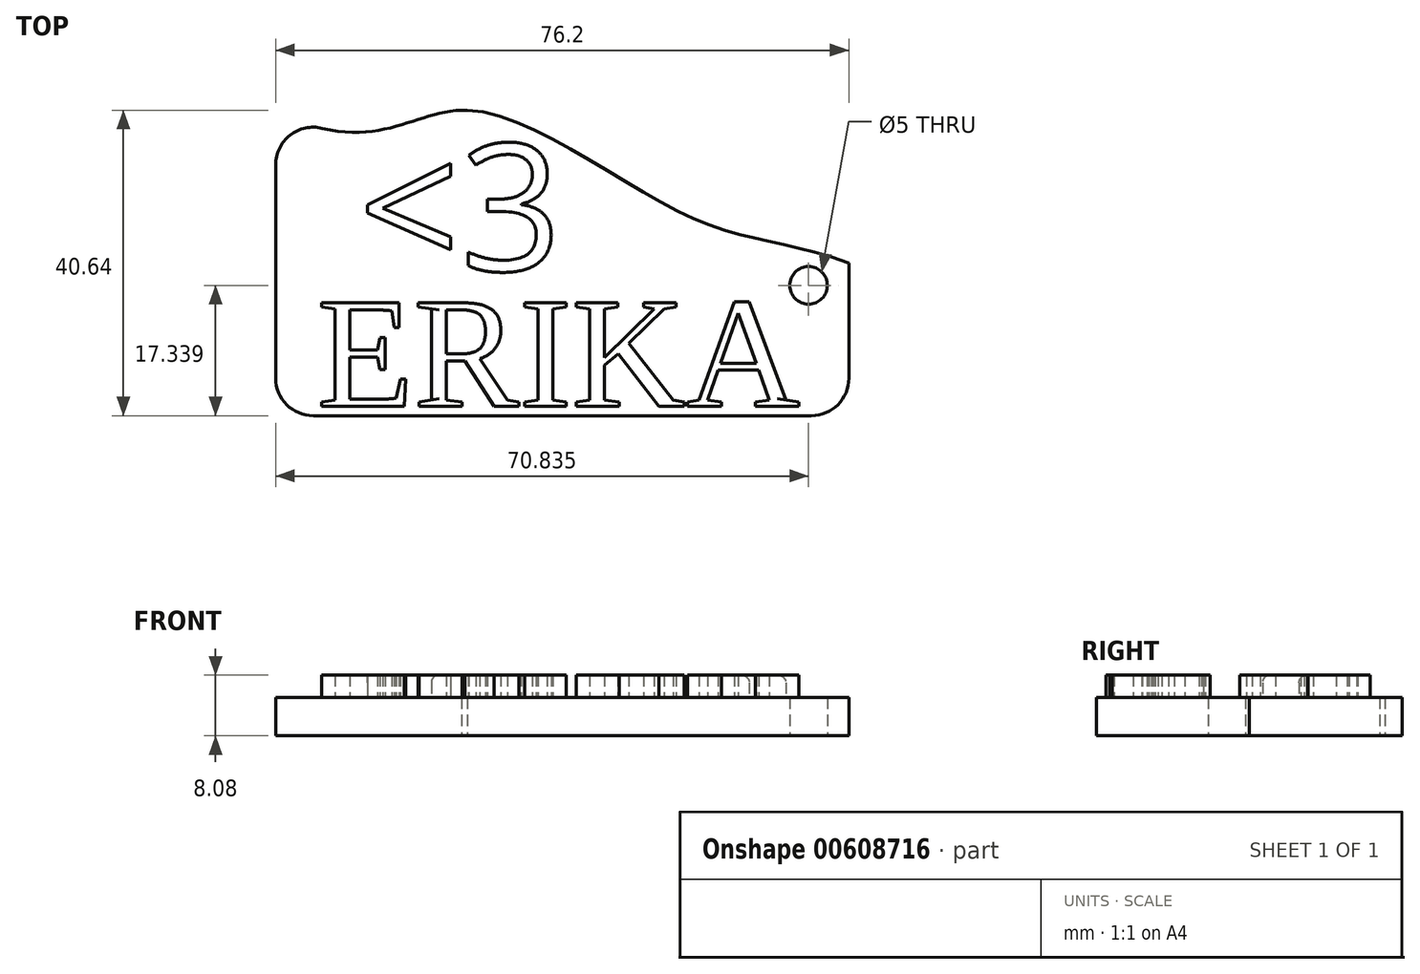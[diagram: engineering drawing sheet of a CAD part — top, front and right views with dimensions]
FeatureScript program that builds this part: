
annotation { "Feature Type Name" : "Feature", "Feature Type Description" : "" }
export const myFeature = defineFeature(function(context is Context, id is Id, definition is map)
    precondition{}
    {
        {
            var Q0;
            Q0=qCreatedBy(makeId("Top.planeOp"),FACE);
            var sketch = newSketch(context, id + "F0", { "sketchPlane" : qUnion([Q0])});
            skLineSegment(sketch, "E0.bottom", {"start": v(0, 0) * mm, "end": v(381, 0) * mm});
            skLineSegment(sketch, "E0.top", {"start": v(0, 203.2) * mm, "end": v(381, 203.2) * mm});
            skLineSegment(sketch, "E0.left", {"start": v(0, 0) * mm, "end": v(0, 203.2) * mm});
            skLineSegment(sketch, "E0.right", {"start": v(381, 0) * mm, "end": v(381, 203.2) * mm});
            skSolve(sketch);
        }
        {
            var Q0;
            Q0=makeQuery(id+"F0.imprint","IMPRINT",FACE,{"disambiguationData":[TD([[makeQuery(id+"F0.imprint","IMPRINT",EDGE,{"derivedFrom":sQuery(id+"F0.wireOp",EDGE,"E0.bottom")}),1.0]])]});
            extrude(context, id + "F1", {"entities" : qUnion([Q0]), "depth" : 25.4 * mm, "offsetDistance" : 25.4 * mm});
        }
        {
            var Q0;
            Q0=makeQuery(id+"F1.opExtrude","CAP_FACE",FACE,{"disambiguationData":[OSD([sQuery(id+"F0.wireOp",EDGE,"E0.bottom"),sQuery(id+"F0.wireOp",EDGE,"E0.top"),sQuery(id+"F0.wireOp",EDGE,"E0.left"),sQuery(id+"F0.wireOp",EDGE,"E0.right")])],"isStart":false});
            var sketch = newSketch(context, id + "F2", { "sketchPlane" : qUnion([Q0])});
            skText(sketch, "E1", { "text": "ERIKA", "fontName": "Tinos-Regular.ttf"});
            const initialGuessF2  = {"E1": [0.02744, 0.00627, 1, 0, 0.07568]};
            skSetInitialGuess(sketch, initialGuessF2);
            skSolve(sketch);
        }
        {
            var Q0;
            Q0=makeQuery(id+"F2.imprint","IMPRINT",FACE,{"disambiguationData":[TD([[makeQuery(id+"F2.imprint","IMPRINT",EDGE,{"derivedFrom":sQuery(id+"F2.wireOp",EDGE,"E1.sketch_text.stroke-26")}),-1.0]])]});
            var Q1;
            Q1=makeQuery(id+"F2.imprint","IMPRINT",FACE,{"disambiguationData":[TD([[makeQuery(id+"F2.imprint","IMPRINT",EDGE,{"derivedFrom":sQuery(id+"F2.wireOp",EDGE,"E1.sketch_text.stroke-53")}),-1.0]])]});
            var Q2;
            Q2=makeQuery(id+"F2.imprint","IMPRINT",FACE,{"disambiguationData":[TD([[makeQuery(id+"F2.imprint","IMPRINT",EDGE,{"derivedFrom":sQuery(id+"F2.wireOp",EDGE,"E1.sketch_text.stroke-65")}),-1.0]])]});
            var Q3;
            Q3=makeQuery(id+"F2.imprint","IMPRINT",FACE,{"disambiguationData":[TD([[makeQuery(id+"F2.imprint","IMPRINT",EDGE,{"derivedFrom":sQuery(id+"F2.wireOp",EDGE,"E1.sketch_text.stroke-91")}),-1.0]])]});
            var Q4;
            Q4=makeQuery(id+"F2.imprint","IMPRINT",FACE,{"disambiguationData":[TD([[makeQuery(id+"F2.imprint","IMPRINT",EDGE,{"derivedFrom":sQuery(id+"F2.wireOp",EDGE,"E1.sketch_text.stroke-0")}),-1.0]])]});
            extrude(context, id + "F3", {"entities" : qUnion([Q0, Q1, Q2, Q3, Q4]), "operationType" : NewBodyOperationType.ADD, "depth" : 15 * mm, "offsetDistance" : 25.4 * mm});
        }
        {
            var Q0;
            {var subQ0=sQuery(id+"F0.wireOp",EDGE,"E0.top");var subQ1=sQuery(id+"F0.wireOp",EDGE,"E0.right");var subQ2=sQuery(id+"F0.wireOp",EDGE,"E0.bottom");var subQ3=sQuery(id+"F0.wireOp",EDGE,"E0.left");Q0=makeQuery(id+"F3.boolean.opBoolean","SPLIT",FACE,{"disambiguationData":[TD([makeQuery(id+"F1.opExtrude","SWEPT_FACE",FACE,{"disambiguationData":[OSD([subQ2])]})])],"derivedFrom":makeQuery(id+"F1.opExtrude","CAP_FACE",FACE,{"disambiguationData":[OSD([subQ2,subQ0,subQ3,subQ1])],"isStart":false})});}
            var sketch = newSketch(context, id + "F4", { "sketchPlane" : qUnion([Q0])});
            skText(sketch, "E2", { "text": "<3", "fontName": "OpenSans-Regular.ttf"});
            const initialGuessF4  = {"E2": [0.055, 0.09643, 1, 0, 0.08502]};
            skSetInitialGuess(sketch, initialGuessF4);
            skSolve(sketch);
        }
        {
            var Q0;
            Q0 = qSketchRegion(id + "F4", true);
            extrude(context, id + "F5", {"entities" : qUnion([Q0]), "operationType" : NewBodyOperationType.ADD, "depth" : 15 * mm, "offsetDistance" : 25.4 * mm});
        }
        {
            var Q0;
            Q0=makeQuery(id+"F1.opExtrude","SWEPT_BODY",BODY,{"disambiguationData":[OSD([sQuery(id+"F0.wireOp",EDGE,"E0.bottom"),sQuery(id+"F0.wireOp",EDGE,"E0.top"),sQuery(id+"F0.wireOp",EDGE,"E0.left"),sQuery(id+"F0.wireOp",EDGE,"E0.right")])]});
            var Q1;
            Q1=qCreatedBy(makeId("Origin.pointOp"),VERTEX);
            transform(context, id + "F6", {"entities" : qUnion([Q0]), "transformType" : TransformType.SCALE_UNIFORMLY, "scale" : 0.2, "scalePoint" : qUnion([Q1]), "makeCopy" : false});
        }
        {
            var Q0;
            Q0=makeQuery(id+"F1.opExtrude","CAP_FACE",FACE,{"disambiguationData":[OSD([sQuery(id+"F0.wireOp",EDGE,"E0.bottom"),sQuery(id+"F0.wireOp",EDGE,"E0.top"),sQuery(id+"F0.wireOp",EDGE,"E0.left"),sQuery(id+"F0.wireOp",EDGE,"E0.right")])],"isStart":true});
            var sketch = newSketch(context, id + "F7", { "sketchPlane" : qUnion([Q0])});
            skPoint(sketch, "E3", {"position": v(76.2, -40.64) * mm});
            skFitSpline(sketch, "E4", {"points": [v(76.2, -20.32) * mm, v(54.58, -26.68) * mm, v(25.49, -40.64) * mm, v(0, -40.64) * mm], "startDerivative": vector(-82.52, -29.2) * mm, "endDerivative": vector(-119.64, -62.23) * mm});
            skLineSegment(sketch, "E5", {"start": v(76.2, -20.32) * mm, "end": v(76.2, -49.02) * mm});
            skLineSegment(sketch, "E6", {"start": v(76.2, -49.02) * mm, "end": v(0, -40.64) * mm});
            skCircle(sketch, "E7", {"center": v(70.83, -17.34) * mm, "radius": 2.5 * mm});
            skSolve(sketch);
        }
        {
            var Q0;
            Q0 = qSketchRegion(id + "F7", true);
            extrude(context, id + "F8", {"entities" : qUnion([Q0]), "operationType" : NewBodyOperationType.REMOVE, "oppositeDirection" : true, "depth" : 25 * mm, "offsetDistance" : 25 * mm});
        }
        {
            var Q0;
            {var subQ0=sQuery(id+"F0.wireOp",EDGE,"E0.left");var subQ1=sQuery(id+"F0.wireOp",EDGE,"E0.top");Q0=makeQuery(id+"F8.boolean.opBoolean","MERGE",EDGE,{"derivedFrom":[makeQuery(id+"F1.opExtrude","SWEPT_EDGE",EDGE,{"disambiguationData":[OSD([subQ1,subQ0])]}),makeQuery(id+"F8.opExtrude","SWEPT_EDGE",EDGE,{"disambiguationData":[OSD([subQ1,subQ0,sQuery(id+"F7.wireOp",EDGE,"E4"),sQuery(id+"F7.wireOp",EDGE,"E6")])]})]});}
            var Q1;
            Q1=makeQuery(id+"F8.boolean.opBoolean","COPY",EDGE,{"derivedFrom":makeQuery(id+"F8.opExtrude","SWEPT_EDGE",EDGE,{"disambiguationData":[OSD([sQuery(id+"F0.wireOp",EDGE,"E0.right"),sQuery(id+"F7.wireOp",EDGE,"E4"),sQuery(id+"F7.wireOp",EDGE,"E5")])]})});
            var Q2;
            Q2=makeQuery(id+"F1.opExtrude","SWEPT_EDGE",EDGE,{"disambiguationData":[OSD([sQuery(id+"F0.wireOp",EDGE,"E0.bottom"),sQuery(id+"F0.wireOp",EDGE,"E0.right")])]});
            var Q3;
            Q3=makeQuery(id+"F1.opExtrude","SWEPT_EDGE",EDGE,{"disambiguationData":[OSD([sQuery(id+"F0.wireOp",EDGE,"E0.bottom"),sQuery(id+"F0.wireOp",EDGE,"E0.left")])]});
            fillet(context, id + "F9", {"entities" : qUnion([Q0, Q1, Q2, Q3]), "radius" : 5 * mm, "tangentPropagation" : true, "allowEdgeOverflow" : false});
        }
        {
            var Q0;
            Q0=makeQuery(id+"F3.opExtrude","CAP_EDGE",EDGE,{"disambiguationData":[OSD([sQuery(id+"F2.wireOp",EDGE,"E1.sketch_text.stroke-97")])],"isStart":false});
            var Q1;
            Q1=makeQuery(id+"F5.opExtrude","CAP_EDGE",EDGE,{"disambiguationData":[OSD([sQuery(id+"F4.wireOp",EDGE,"E2.sketch_text.stroke-0")])],"isStart":false});
            var Q2;
            Q2=makeQuery(id+"F3.opExtrude","CAP_EDGE",EDGE,{"disambiguationData":[OSD([sQuery(id+"F2.wireOp",EDGE,"E1.sketch_text.stroke-32")])],"isStart":false});
            fillet(context, id + "F10", {"entities" : qUnion([Q0, Q1, Q2]), "radius" : 1 * mm, "tangentPropagation" : true, "allowEdgeOverflow" : false});
        }
    });
